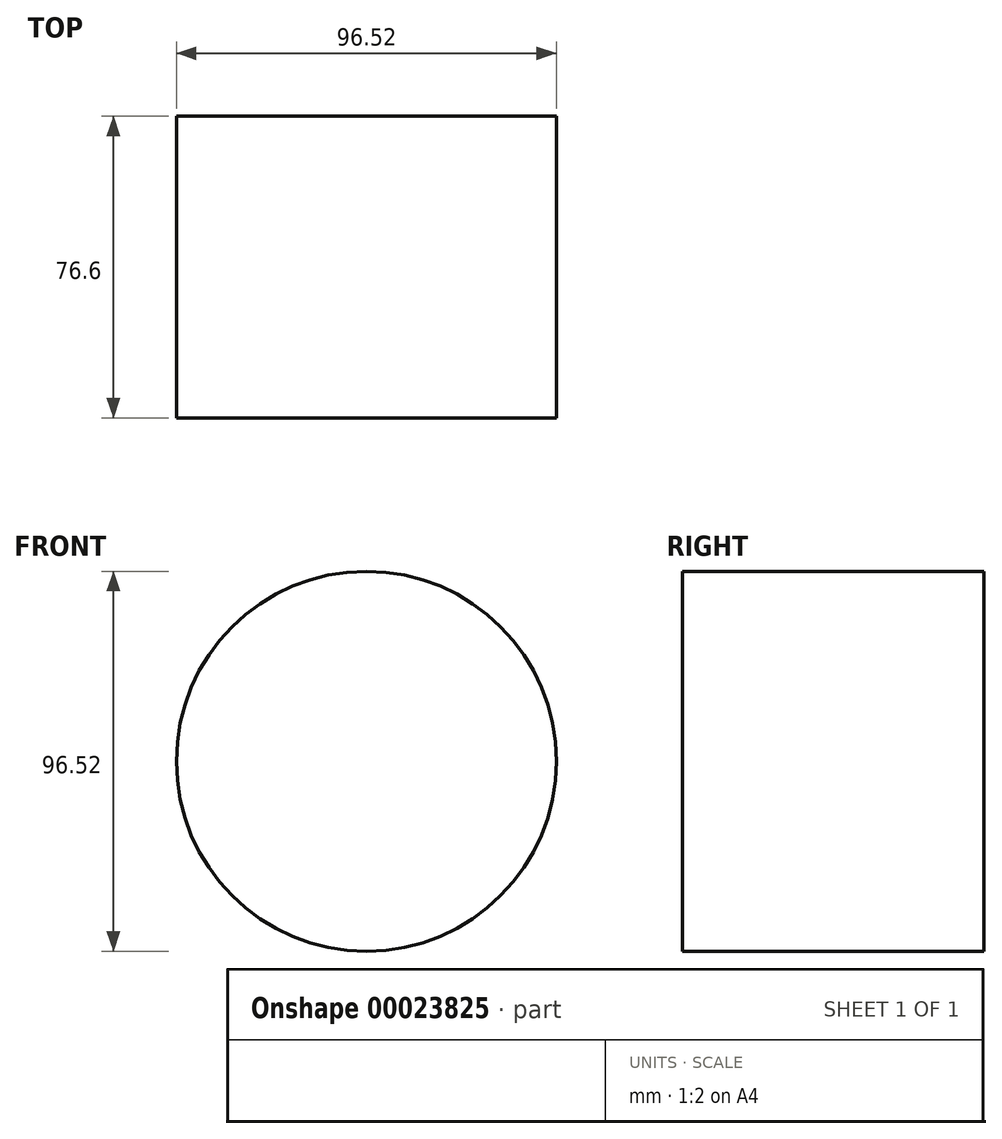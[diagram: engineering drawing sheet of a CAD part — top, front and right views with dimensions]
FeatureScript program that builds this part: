
annotation { "Feature Type Name" : "Feature", "Feature Type Description" : "" }
export const myFeature = defineFeature(function(context is Context, id is Id, definition is map)
    precondition{}
    {
        {
            var Q0;
            Q0=qCreatedBy(makeId("Front.planeOp"),FACE);
            var sketch = newSketch(context, id + "F0", { "sketchPlane" : qUnion([Q0])});
            skCircle(sketch, "E0", {"center": v(0, 0) * mm, "radius": 48.26 * mm});
            skSolve(sketch);
        }
        {
            var Q0;
            Q0 = qSketchRegion(id + "F0", true);
            extrude(context, id + "F1", {"entities" : qUnion([Q0]), "depth" : 76.6 * mm});
        }
    });
